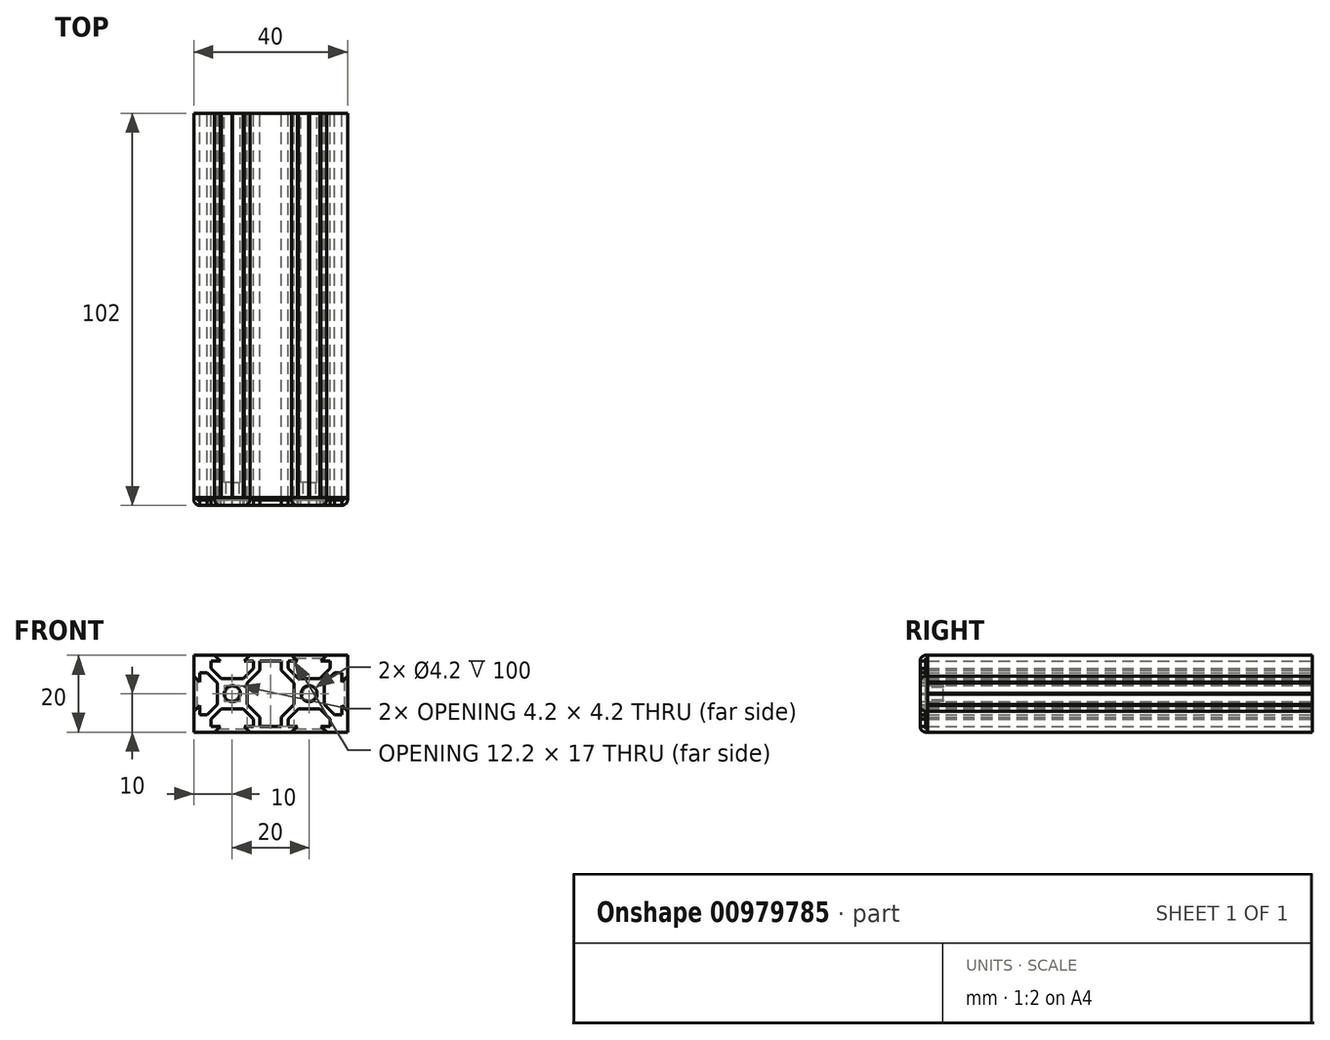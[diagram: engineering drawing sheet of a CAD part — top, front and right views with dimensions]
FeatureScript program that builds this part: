
annotation { "Feature Type Name" : "Feature", "Feature Type Description" : "" }
export const myFeature = defineFeature(function(context is Context, id is Id, definition is map)
    precondition{}
    {
        {
            var Q0;
            Q0=qCreatedBy(makeId("Front.planeOp"),FACE);
            var sketch = newSketch(context, id + "F0", { "sketchPlane" : qUnion([Q0])});
            skLineSegment(sketch, "E0.MirrorCS", {"start": v(-15.5, 8.5) * mm, "end": v(-15.5, 6.56) * mm});
            skLineSegment(sketch, "E1.MirrorCS", {"start": v(-16.56, 5.5) * mm, "end": v(-18.5, 5.5) * mm});
            skLineSegment(sketch, "E2.MirrorCS", {"start": v(-20, 10) * mm, "end": v(-20, 4.6) * mm});
            skLineSegment(sketch, "E3.MirrorCS", {"start": v(-2.8, 6.14) * mm, "end": v(-6.1, 2.84) * mm});
            skLineSegment(sketch, "E4.MirrorCS", {"start": v(-6.1, 2.84) * mm, "end": v(-6.1, 0) * mm});
            skLineSegment(sketch, "E5.MirrorCS", {"start": v(-18.5, 3.1) * mm, "end": v(-20, 4.6) * mm});
            skLineSegment(sketch, "E6.MirrorCS", {"start": v(-15.5, 6.56) * mm, "end": v(-12.84, 3.9) * mm});
            skLineSegment(sketch, "E7.MirrorCS", {"start": v(-13.1, 8.5) * mm, "end": v(-14.6, 10) * mm});
            skLineSegment(sketch, "E8.MirrorCS", {"start": v(-4.5, 8.5) * mm, "end": v(-4.5, 6.56) * mm});
            skLineSegment(sketch, "E9.MirrorCS", {"start": v(-18.5, 5.5) * mm, "end": v(-18.5, 3.1) * mm});
            skLineSegment(sketch, "E10.MirrorCS", {"start": v(-4.5, 6.56) * mm, "end": v(-7.16, 3.9) * mm});
            skLineSegment(sketch, "E11.MirrorCS", {"start": v(-13.9, 2.84) * mm, "end": v(-13.9, 0.1) * mm});
            skLineSegment(sketch, "E12.MirrorCS", {"start": v(-6.9, 8.5) * mm, "end": v(-5.4, 10) * mm});
            skLineSegment(sketch, "E13.MirrorCS", {"start": v(-5.4, 10) * mm, "end": v(0, 10) * mm});
            skLineSegment(sketch, "E14.MirrorCS", {"start": v(-4.5, 8.5) * mm, "end": v(-6.9, 8.5) * mm});
            skLineSegment(sketch, "E15.MirrorCS", {"start": v(-14.6, 10) * mm, "end": v(-20, 10) * mm});
            skLineSegment(sketch, "E16.MirrorCS", {"start": v(-16.56, 5.5) * mm, "end": v(-13.9, 2.84) * mm});
            skLineSegment(sketch, "E17.MirrorCS", {"start": v(-15.5, 8.5) * mm, "end": v(-13.1, 8.5) * mm});
            skLineSegment(sketch, "E18", {"start": v(-2.8, 8.5) * mm, "end": v(-2.8, 6.14) * mm});
            skLineSegment(sketch, "E19", {"start": v(-12.84, 3.9) * mm, "end": v(-10.1, 3.9) * mm});
            skLineSegment(sketch, "E20", {"start": v(-2.8, 8.5) * mm, "end": v(0, 8.5) * mm});
            skLineSegment(sketch, "E21", {"start": v(-12.25, 8.5) * mm, "end": v(-7.9, 8.5) * mm, "construction": true});
            skLineSegment(sketch, "E22", {"start": v(-7.9, 10) * mm, "end": v(-12.25, 10) * mm, "construction": true});
            skArc(sketch, "E23", {"start": v(-7.9, 0) * mm, "mid": v(-10, 2.1) * mm, "end": v(-12.1, 0) * mm});
            skLineSegment(sketch, "E24", {"start": v(-10, 0) * mm, "end": v(-10, 1.07) * mm, "construction": true});
            skLineSegment(sketch, "E25.MirrorCS", {"start": v(-10, 0) * mm, "end": v(-10, -1.07) * mm, "construction": true});
            skLineSegment(sketch, "E26.top", {"start": v(-10.1, 3.7) * mm, "end": v(-9.9, 3.7) * mm});
            skLineSegment(sketch, "E26.left", {"start": v(-10.1, 3.9) * mm, "end": v(-10.1, 3.7) * mm});
            skLineSegment(sketch, "E26.right", {"start": v(-9.9, 3.9) * mm, "end": v(-9.9, 3.7) * mm});
            skLineSegment(sketch, "E27.trimOffspring", {"start": v(-9.9, 3.9) * mm, "end": v(-7.16, 3.9) * mm});
            skLineSegment(sketch, "E28", {"start": v(-13.9, 0.1) * mm, "end": v(-13.7, 0.1) * mm});
            skLineSegment(sketch, "E29", {"start": v(-13.7, 0.1) * mm, "end": v(-13.7, 0) * mm});
            skPoint(sketch, "E30.orphan", {"position": v(-13.9, 0) * mm});
            skLineSegment(sketch, "E31.MirrorCS", {"start": v(13.7, 0.1) * mm, "end": v(13.7, 0) * mm});
            skLineSegment(sketch, "E32.MirrorCS", {"start": v(13.9, 0.1) * mm, "end": v(13.7, 0.1) * mm});
            skLineSegment(sketch, "E33.MirrorCS", {"start": v(10.1, 3.7) * mm, "end": v(9.9, 3.7) * mm});
            skLineSegment(sketch, "E34.MirrorCS", {"start": v(10.1, 3.9) * mm, "end": v(10.1, 3.7) * mm});
            skLineSegment(sketch, "E35.MirrorCS", {"start": v(9.9, 3.9) * mm, "end": v(9.9, 3.7) * mm});
            skLineSegment(sketch, "E36.MirrorCS", {"start": v(20, 10) * mm, "end": v(20, 4.6) * mm});
            skLineSegment(sketch, "E37.MirrorCS", {"start": v(4.5, 6.56) * mm, "end": v(7.16, 3.9) * mm});
            skLineSegment(sketch, "E38.MirrorCS", {"start": v(2.8, 8.5) * mm, "end": v(0, 8.5) * mm});
            skLineSegment(sketch, "E39.MirrorCS", {"start": v(18.5, 5.5) * mm, "end": v(18.5, 3.1) * mm});
            skLineSegment(sketch, "E40.MirrorCS", {"start": v(16.56, 5.5) * mm, "end": v(18.5, 5.5) * mm});
            skLineSegment(sketch, "E41.MirrorCS", {"start": v(15.5, 8.5) * mm, "end": v(15.5, 6.56) * mm});
            skLineSegment(sketch, "E42.MirrorCS", {"start": v(9.9, 3.9) * mm, "end": v(7.16, 3.9) * mm});
            skLineSegment(sketch, "E43.MirrorCS", {"start": v(13.9, 2.84) * mm, "end": v(13.9, 0.1) * mm});
            skLineSegment(sketch, "E44.MirrorCS", {"start": v(15.5, 8.5) * mm, "end": v(13.1, 8.5) * mm});
            skLineSegment(sketch, "E45.MirrorCS", {"start": v(16.56, 5.5) * mm, "end": v(13.9, 2.84) * mm});
            skLineSegment(sketch, "E46.MirrorCS", {"start": v(13.1, 8.5) * mm, "end": v(14.6, 10) * mm});
            skLineSegment(sketch, "E47.MirrorCS", {"start": v(15.5, 6.56) * mm, "end": v(12.84, 3.9) * mm});
            skLineSegment(sketch, "E48.MirrorCS", {"start": v(12.25, 8.5) * mm, "end": v(7.9, 8.5) * mm, "construction": true});
            skLineSegment(sketch, "E49.MirrorCS", {"start": v(12.84, 3.9) * mm, "end": v(10.1, 3.9) * mm});
            skLineSegment(sketch, "E50.MirrorCS", {"start": v(5.4, 10) * mm, "end": v(0, 10) * mm});
            skLineSegment(sketch, "E51.MirrorCS", {"start": v(2.8, 8.5) * mm, "end": v(2.8, 6.14) * mm});
            skLineSegment(sketch, "E52.MirrorCS", {"start": v(4.5, 8.5) * mm, "end": v(4.5, 6.56) * mm});
            skLineSegment(sketch, "E53.MirrorCS", {"start": v(18.5, 3.1) * mm, "end": v(20, 4.6) * mm});
            skPoint(sketch, "E54.MirrorP", {"position": v(13.9, 0) * mm});
            skArc(sketch, "E55.MirrorCS", {"start": v(7.9, 0) * mm, "mid": v(10, 2.1) * mm, "end": v(12.1, 0) * mm});
            skLineSegment(sketch, "E56.MirrorCS", {"start": v(6.1, 2.84) * mm, "end": v(6.1, 0) * mm});
            skLineSegment(sketch, "E57.MirrorCS", {"start": v(14.6, 10) * mm, "end": v(20, 10) * mm});
            skLineSegment(sketch, "E58.MirrorCS", {"start": v(10, 0) * mm, "end": v(10, 1.07) * mm, "construction": true});
            skLineSegment(sketch, "E59.MirrorCS", {"start": v(6.9, 8.5) * mm, "end": v(5.4, 10) * mm});
            skLineSegment(sketch, "E60.MirrorCS", {"start": v(2.8, 6.14) * mm, "end": v(6.1, 2.84) * mm});
            skLineSegment(sketch, "E61.MirrorCS", {"start": v(7.9, 10) * mm, "end": v(12.25, 10) * mm, "construction": true});
            skLineSegment(sketch, "E62.MirrorCS", {"start": v(4.5, 8.5) * mm, "end": v(6.9, 8.5) * mm});
            skLineSegment(sketch, "E63.MirrorCS", {"start": v(13.7, -0.1) * mm, "end": v(13.7, 0) * mm});
            skLineSegment(sketch, "E64.MirrorCS", {"start": v(-13.9, -0.1) * mm, "end": v(-13.7, -0.1) * mm});
            skLineSegment(sketch, "E65.MirrorCS", {"start": v(-13.7, -0.1) * mm, "end": v(-13.7, 0) * mm});
            skLineSegment(sketch, "E66.MirrorCS", {"start": v(13.9, -0.1) * mm, "end": v(13.7, -0.1) * mm});
            skLineSegment(sketch, "E67.MirrorCS", {"start": v(-9.9, -3.9) * mm, "end": v(-9.9, -3.7) * mm});
            skLineSegment(sketch, "E68.MirrorCS", {"start": v(9.9, -3.9) * mm, "end": v(9.9, -3.7) * mm});
            skLineSegment(sketch, "E69.MirrorCS", {"start": v(10.1, -3.9) * mm, "end": v(10.1, -3.7) * mm});
            skLineSegment(sketch, "E70.MirrorCS", {"start": v(10.1, -3.7) * mm, "end": v(9.9, -3.7) * mm});
            skLineSegment(sketch, "E71.MirrorCS", {"start": v(-10.1, -3.7) * mm, "end": v(-9.9, -3.7) * mm});
            skLineSegment(sketch, "E72.MirrorCS", {"start": v(-10.1, -3.9) * mm, "end": v(-10.1, -3.7) * mm});
            skLineSegment(sketch, "E73.MirrorCS", {"start": v(15.5, -6.56) * mm, "end": v(12.84, -3.9) * mm});
            skLineSegment(sketch, "E74.MirrorCS", {"start": v(-18.5, -3.1) * mm, "end": v(-20, -4.6) * mm});
            skLineSegment(sketch, "E75.MirrorCS", {"start": v(2.8, -6.14) * mm, "end": v(6.1, -2.84) * mm});
            skLineSegment(sketch, "E76.MirrorCS", {"start": v(-4.5, -8.5) * mm, "end": v(-6.9, -8.5) * mm});
            skLineSegment(sketch, "E77.MirrorCS", {"start": v(-6.9, -8.5) * mm, "end": v(-5.4, -10) * mm});
            skLineSegment(sketch, "E78.MirrorCS", {"start": v(-15.5, -8.5) * mm, "end": v(-13.1, -8.5) * mm});
            skLineSegment(sketch, "E79.MirrorCS", {"start": v(-12.25, -8.5) * mm, "end": v(-7.9, -8.5) * mm, "construction": true});
            skLineSegment(sketch, "E80.MirrorCS", {"start": v(13.9, -2.84) * mm, "end": v(13.9, -0.1) * mm});
            skLineSegment(sketch, "E81.MirrorCS", {"start": v(-15.5, -8.5) * mm, "end": v(-15.5, -6.56) * mm});
            skLineSegment(sketch, "E82.MirrorCS", {"start": v(-7.9, -10) * mm, "end": v(-12.25, -10) * mm, "construction": true});
            skLineSegment(sketch, "E83.MirrorCS", {"start": v(16.56, -5.5) * mm, "end": v(13.9, -2.84) * mm});
            skArc(sketch, "E84.MirrorCS", {"start": v(-7.9, 0) * mm, "mid": v(-10, -2.1) * mm, "end": v(-12.1, 0) * mm});
            skLineSegment(sketch, "E85.MirrorCS", {"start": v(-2.8, -8.5) * mm, "end": v(-2.8, -6.14) * mm});
            skLineSegment(sketch, "E86.MirrorCS", {"start": v(-16.56, -5.5) * mm, "end": v(-18.5, -5.5) * mm});
            skLineSegment(sketch, "E87.MirrorCS", {"start": v(4.5, -8.5) * mm, "end": v(6.9, -8.5) * mm});
            skLineSegment(sketch, "E88.MirrorCS", {"start": v(14.6, -10) * mm, "end": v(20, -10) * mm});
            skLineSegment(sketch, "E89.MirrorCS", {"start": v(-2.8, -6.14) * mm, "end": v(-6.1, -2.84) * mm});
            skLineSegment(sketch, "E90.MirrorCS", {"start": v(7.9, -10) * mm, "end": v(12.25, -10) * mm, "construction": true});
            skLineSegment(sketch, "E91.MirrorCS", {"start": v(-20, -10) * mm, "end": v(-20, -4.6) * mm});
            skLineSegment(sketch, "E92.MirrorCS", {"start": v(6.9, -8.5) * mm, "end": v(5.4, -10) * mm});
            skLineSegment(sketch, "E93.MirrorCS", {"start": v(4.5, -6.56) * mm, "end": v(7.16, -3.9) * mm});
            skLineSegment(sketch, "E94.MirrorCS", {"start": v(9.9, -3.9) * mm, "end": v(7.16, -3.9) * mm});
            skLineSegment(sketch, "E95.MirrorCS", {"start": v(-12.84, -3.9) * mm, "end": v(-10.1, -3.9) * mm});
            skLineSegment(sketch, "E96.MirrorCS", {"start": v(12.84, -3.9) * mm, "end": v(10.1, -3.9) * mm});
            skLineSegment(sketch, "E97.MirrorCS", {"start": v(-4.5, -6.56) * mm, "end": v(-7.16, -3.9) * mm});
            skLineSegment(sketch, "E98.MirrorCS", {"start": v(20, -10) * mm, "end": v(20, -4.6) * mm});
            skLineSegment(sketch, "E99.MirrorCS", {"start": v(15.5, -8.5) * mm, "end": v(13.1, -8.5) * mm});
            skLineSegment(sketch, "E100.MirrorCS", {"start": v(-13.9, -2.84) * mm, "end": v(-13.9, -0.1) * mm});
            skLineSegment(sketch, "E101.MirrorCS", {"start": v(-5.4, -10) * mm, "end": v(0, -10) * mm});
            skLineSegment(sketch, "E102.MirrorCS", {"start": v(-9.9, -3.9) * mm, "end": v(-7.16, -3.9) * mm});
            skLineSegment(sketch, "E103.MirrorCS", {"start": v(18.5, -5.5) * mm, "end": v(18.5, -3.1) * mm});
            skLineSegment(sketch, "E104.MirrorCS", {"start": v(-2.8, -8.5) * mm, "end": v(0, -8.5) * mm});
            skLineSegment(sketch, "E105.MirrorCS", {"start": v(18.5, -3.1) * mm, "end": v(20, -4.6) * mm});
            skLineSegment(sketch, "E106.MirrorCS", {"start": v(-13.1, -8.5) * mm, "end": v(-14.6, -10) * mm});
            skLineSegment(sketch, "E107.MirrorCS", {"start": v(15.5, -8.5) * mm, "end": v(15.5, -6.56) * mm});
            skLineSegment(sketch, "E108.MirrorCS", {"start": v(-6.1, -2.84) * mm, "end": v(-6.1, 0) * mm});
            skArc(sketch, "E109.MirrorCS", {"start": v(7.9, 0) * mm, "mid": v(10, -2.1) * mm, "end": v(12.1, 0) * mm});
            skLineSegment(sketch, "E110.MirrorCS", {"start": v(10, 0) * mm, "end": v(10, -1.07) * mm, "construction": true});
            skLineSegment(sketch, "E111.MirrorCS", {"start": v(2.8, -8.5) * mm, "end": v(0, -8.5) * mm});
            skLineSegment(sketch, "E112.MirrorCS", {"start": v(6.1, -2.84) * mm, "end": v(6.1, 0) * mm});
            skLineSegment(sketch, "E113.MirrorCS", {"start": v(-16.56, -5.5) * mm, "end": v(-13.9, -2.84) * mm});
            skLineSegment(sketch, "E114.MirrorCS", {"start": v(-18.5, -5.5) * mm, "end": v(-18.5, -3.1) * mm});
            skLineSegment(sketch, "E115.MirrorCS", {"start": v(4.5, -8.5) * mm, "end": v(4.5, -6.56) * mm});
            skLineSegment(sketch, "E116.MirrorCS", {"start": v(-15.5, -6.56) * mm, "end": v(-12.84, -3.9) * mm});
            skLineSegment(sketch, "E117.MirrorCS", {"start": v(5.4, -10) * mm, "end": v(0, -10) * mm});
            skLineSegment(sketch, "E118.MirrorCS", {"start": v(12.25, -8.5) * mm, "end": v(7.9, -8.5) * mm, "construction": true});
            skLineSegment(sketch, "E119.MirrorCS", {"start": v(-4.5, -8.5) * mm, "end": v(-4.5, -6.56) * mm});
            skLineSegment(sketch, "E120.MirrorCS", {"start": v(13.1, -8.5) * mm, "end": v(14.6, -10) * mm});
            skLineSegment(sketch, "E121.MirrorCS", {"start": v(2.8, -8.5) * mm, "end": v(2.8, -6.14) * mm});
            skLineSegment(sketch, "E122.MirrorCS", {"start": v(16.56, -5.5) * mm, "end": v(18.5, -5.5) * mm});
            skLineSegment(sketch, "E123.MirrorCS", {"start": v(-14.6, -10) * mm, "end": v(-20, -10) * mm});
            skSolve(sketch);
        }
        {
            var Q0;
            Q0=makeQuery(id+"F0.imprint","IMPRINT",FACE,{"disambiguationData":[TD([[makeQuery(id+"F0.imprint","IMPRINT",EDGE,{"derivedFrom":sQuery(id+"F0.wireOp",EDGE,"E0.MirrorCS")}),-1.0]])]});
            extrude(context, id + "F1", {"entities" : qUnion([Q0]), "depth" : 100 * mm, "offsetDistance" : 25 * mm, "symmetric" : true});
        }
        {
            var Q0;
            Q0=makeQuery(id+"F1.opExtrude","CAP_FACE",FACE,{"disambiguationData":[OSD([sQuery(id+"F0.wireOp",EDGE,"E0.MirrorCS"),sQuery(id+"F0.wireOp",EDGE,"E1.MirrorCS"),sQuery(id+"F0.wireOp",EDGE,"E2.MirrorCS"),sQuery(id+"F0.wireOp",EDGE,"E3.MirrorCS"),sQuery(id+"F0.wireOp",EDGE,"E4.MirrorCS"),sQuery(id+"F0.wireOp",EDGE,"E5.MirrorCS"),sQuery(id+"F0.wireOp",EDGE,"E6.MirrorCS"),sQuery(id+"F0.wireOp",EDGE,"E7.MirrorCS"),sQuery(id+"F0.wireOp",EDGE,"E8.MirrorCS"),sQuery(id+"F0.wireOp",EDGE,"E9.MirrorCS"),sQuery(id+"F0.wireOp",EDGE,"E10.MirrorCS"),sQuery(id+"F0.wireOp",EDGE,"E11.MirrorCS"),sQuery(id+"F0.wireOp",EDGE,"E12.MirrorCS"),sQuery(id+"F0.wireOp",EDGE,"E13.MirrorCS"),sQuery(id+"F0.wireOp",EDGE,"E14.MirrorCS"),sQuery(id+"F0.wireOp",EDGE,"E15.MirrorCS"),sQuery(id+"F0.wireOp",EDGE,"E16.MirrorCS"),sQuery(id+"F0.wireOp",EDGE,"E17.MirrorCS"),sQuery(id+"F0.wireOp",EDGE,"E18"),sQuery(id+"F0.wireOp",EDGE,"E19"),sQuery(id+"F0.wireOp",EDGE,"E20"),sQuery(id+"F0.wireOp",EDGE,"E23"),sQuery(id+"F0.wireOp",EDGE,"E26.top"),sQuery(id+"F0.wireOp",EDGE,"E26.left"),sQuery(id+"F0.wireOp",EDGE,"E26.right"),sQuery(id+"F0.wireOp",EDGE,"E27.trimOffspring"),sQuery(id+"F0.wireOp",EDGE,"E28"),sQuery(id+"F0.wireOp",EDGE,"E29"),sQuery(id+"F0.wireOp",EDGE,"E31.MirrorCS"),sQuery(id+"F0.wireOp",EDGE,"E32.MirrorCS"),sQuery(id+"F0.wireOp",EDGE,"E33.MirrorCS"),sQuery(id+"F0.wireOp",EDGE,"E34.MirrorCS"),sQuery(id+"F0.wireOp",EDGE,"E35.MirrorCS"),sQuery(id+"F0.wireOp",EDGE,"E36.MirrorCS"),sQuery(id+"F0.wireOp",EDGE,"E37.MirrorCS"),sQuery(id+"F0.wireOp",EDGE,"E38.MirrorCS"),sQuery(id+"F0.wireOp",EDGE,"E39.MirrorCS"),sQuery(id+"F0.wireOp",EDGE,"E40.MirrorCS"),sQuery(id+"F0.wireOp",EDGE,"E41.MirrorCS"),sQuery(id+"F0.wireOp",EDGE,"E42.MirrorCS"),sQuery(id+"F0.wireOp",EDGE,"E43.MirrorCS"),sQuery(id+"F0.wireOp",EDGE,"E44.MirrorCS"),sQuery(id+"F0.wireOp",EDGE,"E45.MirrorCS"),sQuery(id+"F0.wireOp",EDGE,"E46.MirrorCS"),sQuery(id+"F0.wireOp",EDGE,"E47.MirrorCS"),sQuery(id+"F0.wireOp",EDGE,"E49.MirrorCS"),sQuery(id+"F0.wireOp",EDGE,"E50.MirrorCS"),sQuery(id+"F0.wireOp",EDGE,"E51.MirrorCS"),sQuery(id+"F0.wireOp",EDGE,"E52.MirrorCS"),sQuery(id+"F0.wireOp",EDGE,"E53.MirrorCS"),sQuery(id+"F0.wireOp",EDGE,"E55.MirrorCS"),sQuery(id+"F0.wireOp",EDGE,"E56.MirrorCS"),sQuery(id+"F0.wireOp",EDGE,"E57.MirrorCS"),sQuery(id+"F0.wireOp",EDGE,"E59.MirrorCS"),sQuery(id+"F0.wireOp",EDGE,"E60.MirrorCS"),sQuery(id+"F0.wireOp",EDGE,"E62.MirrorCS"),sQuery(id+"F0.wireOp",EDGE,"E63.MirrorCS"),sQuery(id+"F0.wireOp",EDGE,"E64.MirrorCS"),sQuery(id+"F0.wireOp",EDGE,"E65.MirrorCS"),sQuery(id+"F0.wireOp",EDGE,"E66.MirrorCS"),sQuery(id+"F0.wireOp",EDGE,"E67.MirrorCS"),sQuery(id+"F0.wireOp",EDGE,"E68.MirrorCS"),sQuery(id+"F0.wireOp",EDGE,"E69.MirrorCS"),sQuery(id+"F0.wireOp",EDGE,"E70.MirrorCS"),sQuery(id+"F0.wireOp",EDGE,"E71.MirrorCS"),sQuery(id+"F0.wireOp",EDGE,"E72.MirrorCS"),sQuery(id+"F0.wireOp",EDGE,"E73.MirrorCS"),sQuery(id+"F0.wireOp",EDGE,"E74.MirrorCS"),sQuery(id+"F0.wireOp",EDGE,"E75.MirrorCS"),sQuery(id+"F0.wireOp",EDGE,"E76.MirrorCS"),sQuery(id+"F0.wireOp",EDGE,"E77.MirrorCS"),sQuery(id+"F0.wireOp",EDGE,"E78.MirrorCS"),sQuery(id+"F0.wireOp",EDGE,"E80.MirrorCS"),sQuery(id+"F0.wireOp",EDGE,"E81.MirrorCS"),sQuery(id+"F0.wireOp",EDGE,"E83.MirrorCS"),sQuery(id+"F0.wireOp",EDGE,"E84.MirrorCS"),sQuery(id+"F0.wireOp",EDGE,"E85.MirrorCS"),sQuery(id+"F0.wireOp",EDGE,"E86.MirrorCS"),sQuery(id+"F0.wireOp",EDGE,"E87.MirrorCS"),sQuery(id+"F0.wireOp",EDGE,"E88.MirrorCS"),sQuery(id+"F0.wireOp",EDGE,"E89.MirrorCS"),sQuery(id+"F0.wireOp",EDGE,"E91.MirrorCS"),sQuery(id+"F0.wireOp",EDGE,"E92.MirrorCS"),sQuery(id+"F0.wireOp",EDGE,"E93.MirrorCS"),sQuery(id+"F0.wireOp",EDGE,"E94.MirrorCS"),sQuery(id+"F0.wireOp",EDGE,"E95.MirrorCS"),sQuery(id+"F0.wireOp",EDGE,"E96.MirrorCS"),sQuery(id+"F0.wireOp",EDGE,"E97.MirrorCS"),sQuery(id+"F0.wireOp",EDGE,"E98.MirrorCS"),sQuery(id+"F0.wireOp",EDGE,"E99.MirrorCS"),sQuery(id+"F0.wireOp",EDGE,"E100.MirrorCS"),sQuery(id+"F0.wireOp",EDGE,"E101.MirrorCS"),sQuery(id+"F0.wireOp",EDGE,"E102.MirrorCS"),sQuery(id+"F0.wireOp",EDGE,"E103.MirrorCS"),sQuery(id+"F0.wireOp",EDGE,"E104.MirrorCS"),sQuery(id+"F0.wireOp",EDGE,"E105.MirrorCS"),sQuery(id+"F0.wireOp",EDGE,"E106.MirrorCS"),sQuery(id+"F0.wireOp",EDGE,"E107.MirrorCS"),sQuery(id+"F0.wireOp",EDGE,"E108.MirrorCS"),sQuery(id+"F0.wireOp",EDGE,"E109.MirrorCS"),sQuery(id+"F0.wireOp",EDGE,"E111.MirrorCS"),sQuery(id+"F0.wireOp",EDGE,"E112.MirrorCS"),sQuery(id+"F0.wireOp",EDGE,"E113.MirrorCS"),sQuery(id+"F0.wireOp",EDGE,"E114.MirrorCS"),sQuery(id+"F0.wireOp",EDGE,"E115.MirrorCS"),sQuery(id+"F0.wireOp",EDGE,"E116.MirrorCS"),sQuery(id+"F0.wireOp",EDGE,"E117.MirrorCS"),sQuery(id+"F0.wireOp",EDGE,"E119.MirrorCS"),sQuery(id+"F0.wireOp",EDGE,"E120.MirrorCS"),sQuery(id+"F0.wireOp",EDGE,"E121.MirrorCS"),sQuery(id+"F0.wireOp",EDGE,"E122.MirrorCS"),sQuery(id+"F0.wireOp",EDGE,"E123.MirrorCS")])],"isStart":false});
            var sketch = newSketch(context, id + "F2", { "sketchPlane" : qUnion([Q0])});
            skLineSegment(sketch, "E124.bottom", {"start": v(-20, 10) * mm, "end": v(20, 10) * mm});
            skLineSegment(sketch, "E124.top", {"start": v(-20, -10) * mm, "end": v(20, -10) * mm});
            skLineSegment(sketch, "E124.left", {"start": v(-20, 10) * mm, "end": v(-20, -10) * mm});
            skLineSegment(sketch, "E124.right", {"start": v(20, 10) * mm, "end": v(20, -10) * mm});
            skCircle(sketch, "E125", {"center": v(-10, 0) * mm, "radius": 2.1 * mm});
            skCircle(sketch, "E126", {"center": v(10, 0) * mm, "radius": 2.1 * mm});
            skCircle(sketch, "E127", {"center": v(10, 0) * mm, "radius": 1.7 * mm});
            skCircle(sketch, "E128", {"center": v(-10, 0) * mm, "radius": 1.7 * mm});
            skLineSegment(sketch, "E129", {"start": v(-9.8, 2.62) * mm, "end": v(-9.8, -2.99) * mm, "construction": true});
            skLineSegment(sketch, "E130", {"start": v(-10.2, -2.99) * mm, "end": v(-10.2, 2.62) * mm, "construction": true});
            skLineSegment(sketch, "E131", {"start": v(-8.97, 0) * mm, "end": v(-11.03, 0) * mm, "construction": true});
            skLineSegment(sketch, "E132", {"start": v(-10, -0.54) * mm, "end": v(-10, 0.54) * mm, "construction": true});
            skLineSegment(sketch, "E133", {"start": v(10, 1) * mm, "end": v(10, -1) * mm, "construction": true});
            skLineSegment(sketch, "E134", {"start": v(9.04, 0) * mm, "end": v(10.96, 0) * mm, "construction": true});
            skLineSegment(sketch, "E135", {"start": v(10.2, 2.97) * mm, "end": v(10.2, -2.76) * mm, "construction": true});
            skLineSegment(sketch, "E136", {"start": v(9.8, -2.76) * mm, "end": v(9.8, 2.97) * mm, "construction": true});
            skLineSegment(sketch, "E137", {"start": v(-10.2, 2.1) * mm, "end": v(-10.2, 1.69) * mm});
            skLineSegment(sketch, "E138", {"start": v(-10.2, -1.69) * mm, "end": v(-10.2, -2.1) * mm});
            skLineSegment(sketch, "E139", {"start": v(-9.8, 2.1) * mm, "end": v(-9.8, 1.69) * mm});
            skLineSegment(sketch, "E140", {"start": v(-9.8, -1.69) * mm, "end": v(-9.8, -2.1) * mm});
            skLineSegment(sketch, "E141", {"start": v(9.8, 2.1) * mm, "end": v(9.8, 1.69) * mm});
            skLineSegment(sketch, "E142", {"start": v(9.8, -1.69) * mm, "end": v(9.8, -2.1) * mm});
            skLineSegment(sketch, "E143", {"start": v(10.2, 2.1) * mm, "end": v(10.2, 1.69) * mm});
            skLineSegment(sketch, "E144", {"start": v(10.2, -1.69) * mm, "end": v(10.2, -2.1) * mm});
            skSolve(sketch);
        }
        {
            var Q0;
            Q0=makeQuery(id+"F2.imprint","IMPRINT",FACE,{"disambiguationData":[TD([[makeQuery(id+"F2.imprint","IMPRINT",EDGE,{"derivedFrom":makeQuery(id+"F1.opExtrude","CAP_EDGE",EDGE,{"disambiguationData":[OSD([sQuery(id+"F0.wireOp",EDGE,"E0.MirrorCS")])],"isStart":false})}),1.0]])]});
            var Q1;
            Q1=makeQuery(id+"F2.imprint","IMPRINT",FACE,{"disambiguationData":[TD([[makeQuery(id+"F2.imprint","IMPRINT",EDGE,{"derivedFrom":makeQuery(id+"F1.opExtrude","CAP_EDGE",EDGE,{"disambiguationData":[OSD([sQuery(id+"F0.wireOp",EDGE,"E3.MirrorCS")])],"isStart":false})}),1.0]])]});
            var Q2;
            Q2=makeQuery(id+"F2.imprint","IMPRINT",FACE,{"disambiguationData":[TD([[makeQuery(id+"F2.imprint","IMPRINT",EDGE,{"derivedFrom":makeQuery(id+"F1.opExtrude","CAP_EDGE",EDGE,{"disambiguationData":[OSD([sQuery(id+"F0.wireOp",EDGE,"E33.MirrorCS")])],"isStart":false})}),-1.0]])]});
            var Q3;
            Q3=makeQuery(id+"F2.imprint","IMPRINT",FACE,{"disambiguationData":[TD([[makeQuery(id+"F2.imprint","IMPRINT",EDGE,{"derivedFrom":makeQuery(id+"F1.opExtrude","CAP_EDGE",EDGE,{"disambiguationData":[OSD([sQuery(id+"F0.wireOp",EDGE,"E32.MirrorCS")])],"isStart":false})}),1.0]])]});
            var Q4;
            Q4=makeQuery(id+"F2.imprint","IMPRINT",FACE,{"disambiguationData":[TD([[makeQuery(id+"F2.imprint","IMPRINT",EDGE,{"derivedFrom":sQuery(id+"F2.wireOp",EDGE,"E125")}),-1.0]])]});
            var Q5;
            Q5=makeQuery(id+"F2.imprint","IMPRINT",FACE,{"disambiguationData":[TD([[makeQuery(id+"F2.imprint","IMPRINT",EDGE,{"derivedFrom":makeQuery(id+"F1.opExtrude","CAP_EDGE",EDGE,{"disambiguationData":[OSD([sQuery(id+"F0.wireOp",EDGE,"E68.MirrorCS")])],"isStart":false})}),-1.0]])]});
            var Q6;
            Q6=makeQuery(id+"F2.imprint","IMPRINT",FACE,{"disambiguationData":[TD([[makeQuery(id+"F2.imprint","IMPRINT",EDGE,{"derivedFrom":makeQuery(id+"F1.opExtrude","CAP_EDGE",EDGE,{"disambiguationData":[OSD([sQuery(id+"F0.wireOp",EDGE,"E67.MirrorCS")])],"isStart":false})}),1.0]])]});
            var Q7;
            Q7=makeQuery(id+"F2.imprint","IMPRINT",FACE,{"disambiguationData":[TD([[makeQuery(id+"F2.imprint","IMPRINT",EDGE,{"derivedFrom":makeQuery(id+"F1.opExtrude","CAP_EDGE",EDGE,{"disambiguationData":[OSD([sQuery(id+"F0.wireOp",EDGE,"E1.MirrorCS")])],"isStart":false})}),1.0]])]});
            var Q8;
            Q8=makeQuery(id+"F2.imprint","IMPRINT",FACE,{"disambiguationData":[TD([[makeQuery(id+"F2.imprint","IMPRINT",EDGE,{"derivedFrom":sQuery(id+"F2.wireOp",EDGE,"E126")}),1.0]])]});
            var Q9;
            Q9=makeQuery(id+"F2.imprint","IMPRINT",FACE,{"disambiguationData":[TD([[makeQuery(id+"F2.imprint","IMPRINT",EDGE,{"derivedFrom":sQuery(id+"F2.wireOp",EDGE,"E125")}),1.0]])]});
            var Q10;
            {var subQ0=sQuery(id+"F2.wireOp",EDGE,"E128");var subQ1=makeQuery(id+"F2.imprint","INTERSECT",VERTEX,{"derivedFrom":[subQ0,sQuery(id+"F2.wireOp",EDGE,"E137")]});Q10=makeQuery(id+"F2.imprint","IMPRINT",FACE,{"disambiguationData":[TD([[makeQuery(id+"F2.imprint","IMPRINT",EDGE,{"disambiguationData":[TD([[subQ1,1.0]])],"derivedFrom":subQ0}),1.0]])]});}
            var Q11;
            {var subQ0=sQuery(id+"F2.wireOp",EDGE,"E127");var subQ1=makeQuery(id+"F2.imprint","INTERSECT",VERTEX,{"derivedFrom":[subQ0,sQuery(id+"F2.wireOp",EDGE,"E141")]});Q11=makeQuery(id+"F2.imprint","IMPRINT",FACE,{"disambiguationData":[TD([[makeQuery(id+"F2.imprint","IMPRINT",EDGE,{"disambiguationData":[TD([[subQ1,1.0]])],"derivedFrom":subQ0}),1.0]])]});}
            extrude(context, id + "F3", {"entities" : qUnion([Q0, Q1, Q2, Q3, Q4, Q5, Q6, Q7, Q8, Q9, Q10, Q11]), "depth" : 2 * mm, "offsetDistance" : 25 * mm});
        }
        {
            var Q0;
            Q0=makeQuery(id+"F3.opExtrude","CAP_FACE",FACE,{"disambiguationData":[OSD([sQuery(id+"F2.wireOp",EDGE,"E124.bottom"),sQuery(id+"F2.wireOp",EDGE,"E124.top"),sQuery(id+"F2.wireOp",EDGE,"E124.left"),sQuery(id+"F2.wireOp",EDGE,"E124.right")])],"isStart":true});
            var sketch = newSketch(context, id + "F4", { "sketchPlane" : qUnion([Q0])});
            skLineSegment(sketch, "E145.0", {"start": v(-19.2, 9.2) * mm, "end": v(-19.2, -9.2) * mm});
            skLineSegment(sketch, "E145.1", {"start": v(19.2, 9.2) * mm, "end": v(-19.2, 9.2) * mm});
            skLineSegment(sketch, "E145.2", {"start": v(19.2, 9.2) * mm, "end": v(19.2, -9.2) * mm});
            skLineSegment(sketch, "E145.3", {"start": v(19.2, -9.2) * mm, "end": v(-19.2, -9.2) * mm});
            skSolve(sketch);
        }
        {
            var Q0;
            Q0=makeQuery(id+"F4.imprint","IMPRINT",FACE,{"disambiguationData":[TD([[makeQuery(id+"F4.imprint","IMPRINT",EDGE,{"derivedFrom":sQuery(id+"F4.wireOp",EDGE,"E145.0")}),1.0]])]});
            extrude(context, id + "F5", {"entities" : qUnion([Q0]), "operationType" : NewBodyOperationType.REMOVE, "oppositeDirection" : true, "depth" : 0.6 * mm, "offsetDistance" : 25 * mm});
        }
        {
            var Q0;
            {var subQ0=sQuery(id+"F2.wireOp",EDGE,"E143");Q0=makeQuery(id+"F2.imprint","IMPRINT",FACE,{"disambiguationData":[TD([[makeQuery(id+"F2.imprint","IMPRINT",EDGE,{"derivedFrom":subQ0}),1.0]])]});}
            var Q1;
            {var subQ0=sQuery(id+"F2.wireOp",EDGE,"E141");Q1=makeQuery(id+"F2.imprint","IMPRINT",FACE,{"disambiguationData":[TD([[makeQuery(id+"F2.imprint","IMPRINT",EDGE,{"derivedFrom":subQ0}),-1.0]])]});}
            var Q2;
            {var subQ0=sQuery(id+"F2.wireOp",EDGE,"E139");Q2=makeQuery(id+"F2.imprint","IMPRINT",FACE,{"disambiguationData":[TD([[makeQuery(id+"F2.imprint","IMPRINT",EDGE,{"derivedFrom":subQ0}),1.0]])]});}
            var Q3;
            {var subQ0=sQuery(id+"F2.wireOp",EDGE,"E137");Q3=makeQuery(id+"F2.imprint","IMPRINT",FACE,{"disambiguationData":[TD([[makeQuery(id+"F2.imprint","IMPRINT",EDGE,{"derivedFrom":subQ0}),-1.0]])]});}
            extrude(context, id + "F6", {"entities" : qUnion([Q0, Q1, Q2, Q3]), "operationType" : NewBodyOperationType.ADD, "oppositeDirection" : true, "depth" : 4 * mm, "offsetDistance" : 25 * mm, "hasSecondDirection" : true, "secondDirectionOppositeDirection" : false, "secondDirectionDepth" : 1 * mm});
        }
        {
            var Q0;
            Q0=makeQuery(id+"F3.opExtrude","CAP_EDGE",EDGE,{"disambiguationData":[OSD([sQuery(id+"F2.wireOp",EDGE,"E124.bottom")])],"isStart":false});
            var Q1;
            Q1=makeQuery(id+"F3.opExtrude","CAP_EDGE",EDGE,{"disambiguationData":[OSD([sQuery(id+"F2.wireOp",EDGE,"E124.left")])],"isStart":false});
            var Q2;
            Q2=makeQuery(id+"F3.opExtrude","CAP_EDGE",EDGE,{"disambiguationData":[OSD([sQuery(id+"F2.wireOp",EDGE,"E124.top")])],"isStart":false});
            var Q3;
            Q3=makeQuery(id+"F3.opExtrude","CAP_EDGE",EDGE,{"disambiguationData":[OSD([sQuery(id+"F2.wireOp",EDGE,"E124.right")])],"isStart":false});
            fillet(context, id + "F7", {"entities" : qUnion([Q0, Q1, Q2, Q3]), "radius" : 1.5 * mm, "tangentPropagation" : true, "allowEdgeOverflow" : false});
        }
    });
